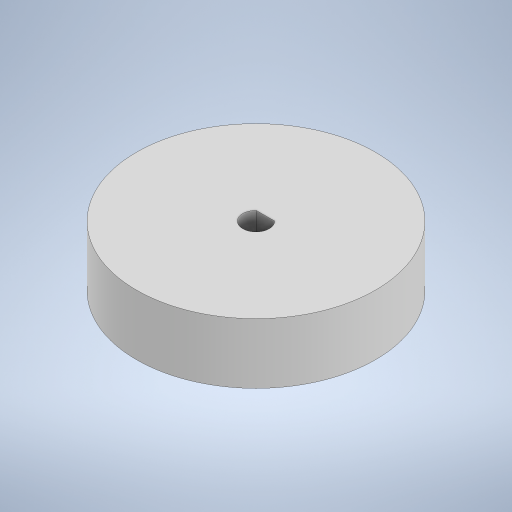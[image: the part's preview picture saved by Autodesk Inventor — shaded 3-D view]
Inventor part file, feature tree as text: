
AUTODESK INVENTOR PART (.ipt)
format: ipt  version: 2023 (Build 270158000, 158)  size: 262,144 bytes
history: native  units: in
note: dims shown in document units (in); Inventor stores cm internally (conversion verified against a paired STEP export)
features: extrude x1, sketch x1
ambient origin geometry x8: Origin, YZ Plane, XZ Plane, XY Plane, X Axis, Y Axis, Z Axis, Center Point
bodies: Body1 (feature_tree)
feature tree (2):
  extrude  "Extrusion2"  Depth=0.4724in
  sketch  "Sketch1"  dims[d0=1.8701in d1=0.2067in d2=0.1772in d22=5.9055in d24=360.0deg d26=0.4724in d27=0.0in]
